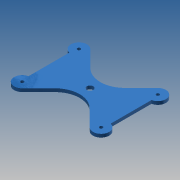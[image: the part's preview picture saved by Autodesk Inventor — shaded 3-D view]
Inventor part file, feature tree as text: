
AUTODESK INVENTOR PART (.ipt)
format: ipt  version: 2017 (Build 210142000, 142)  size: 115,712 bytes
history: native  units: mm
features: other x4, reference x4, extrude x1, sketch x1
ambient origin geometry x8: Origin, YZ Plane, XZ Plane, XY Plane, X Axis, Y Axis, Z Axis, Center Point
bodies: Body1 (feature_tree)
feature tree (10):
  other  "Sólido1"
  extrude  "Extrusión1"  Depth=30.0mm
  sketch  "Boceto1"  dims[d0=10.0mm d1=8.0mm d2=4.0mm d3=0.0mm d4=10.0mm d5=30.0mm d6=8.0mm d7=90.0deg]
  reference  "Referencia1"
  reference  "Referencia2"
  reference  "Referencia3"
  reference  "Referencia5"
  other  "<userpath>\Documents\GitHub\actor-re-actor\models\inventor-caja\Case\CaseC.iam"
  other  "CaseC.iam"
  other  "Pliegue Principal:1"
